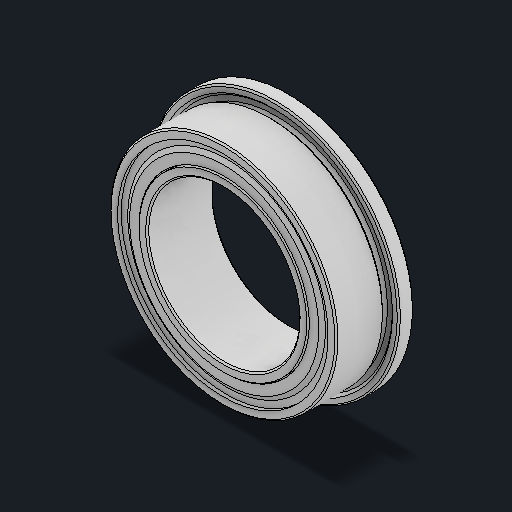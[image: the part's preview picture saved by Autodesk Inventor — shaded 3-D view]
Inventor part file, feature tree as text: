
AUTODESK INVENTOR PART (.ipt)
format: ipt  version: 2024 (Build 280153000, 153)  size: 990,720 bytes
history: native  units: in
note: dims shown in document units (in); Inventor stores cm internally (conversion verified against a paired STEP export)
features: other x23, revolve x3
ambient origin geometry x8: Origin, YZ Plane, XZ Plane, XY Plane, X Axis, Y Axis, Z Axis, Center Point
bodies: Solid1 (feature_tree), Solid2 (feature_tree), Solid3 (feature_tree), Solid4 (feature_tree), Solid5 (feature_tree), Solid6 (feature_tree), Solid7 (feature_tree), Solid8 (feature_tree), Solid9 (feature_tree), Solid10 (feature_tree), Solid11 (feature_tree), Solid12 (feature_tree), Solid13 (feature_tree), Solid14 (feature_tree), Solid15 (feature_tree), Solid16 (feature_tree), Solid17 (feature_tree), Solid18 (feature_tree), Solid19 (feature_tree), Solid20 (feature_tree), Solid21 (feature_tree), Solid22 (feature_tree), Solid23 (feature_tree), Solid24 (feature_tree), Solid25 (feature_tree), Solid26 (feature_tree)
feature tree (26):
  revolve  "Revolve3"  [1 undecoded]
  other  "CirPattern3[1]"
  other  "CirPattern3[2]"
  other  "CirPattern3[3]"
  other  "CirPattern3[4]"
  other  "CirPattern3[5]"
  other  "CirPattern3[6]"
  other  "CirPattern3[7]"
  other  "CirPattern3[8]"
  other  "CirPattern3[9]"
  other  "CirPattern3[10]"
  other  "CirPattern3[11]"
  other  "Cut-Revolve1[1]"
  other  "Cut-Revolve1[2]"
  revolve  "Revolve4[1]"  [1 undecoded]
  revolve  "Revolve4[2]"  [1 undecoded]
  other  "CirPattern3[12]"
  other  "CirPattern3[13]"
  other  "CirPattern3[14]"
  other  "CirPattern3[15]"
  other  "CirPattern3[16]"
  other  "CirPattern3[17]"
  other  "CirPattern3[18]"
  other  "CirPattern3[19]"
  other  "CirPattern3[20]"
  other  "CirPattern3[21]"
note: 3 required parameter values undecoded (feature->parameter linkage not recoverable at this tier; creation-order binding heuristic only, values carry confidence <= 0.55)
